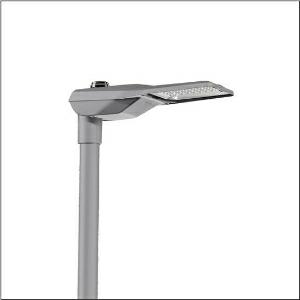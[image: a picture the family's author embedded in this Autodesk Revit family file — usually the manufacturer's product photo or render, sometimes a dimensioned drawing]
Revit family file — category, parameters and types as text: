
# Revit family: streetlight_sl_21_mini___pl52_5xe6h47n08hb_96c1
name_source: partatom
category: Lighting Fixtures
units: mm (PartAtom-declared; Revit-internal decimal feet)

## family parameters
Cut with Voids When Loaded = No
Host = Face
Light Source = No
Part Type = Normal
Room Calculation Point = No
Round Connector Dimension = Use Diameter
Shared = No

## types (1)
- --- (1 x LED, 9260 lm, 66 W, 4000K)
    Apparent Load = 66 VA
    CIE Flux Codes = 27 59 98 100 100
    Color Rendering = 70
    Color Temperature = 4000K
    Default Elevation = 1800 mm
    Description = Streetlight SL 21 mini, mast luminaire, primary light control with lens, of PMMA, primary optical cover: cover, of toughened safety glass, transparent, light distribution: PL52, light emission: direct distribution, primary light characteristic: asymmetric, installation type: side-entry, LED, 3G 1.5mm², High Power LED, rated luminous flux: 9.260lm, luminous efficacy: 140lm/W, light colour: 740, colour temperature: 4000K, control gear: NEMA (7pin), control: overheat protection, pre-setting: linear dimming characteristic, constant luminous flux control, time-dependent luminous flux control, flexible luminous flux parameterisation, mains connection: 230..240V, AC, 50/60Hz, connection cable pre-assembled, cable length: 8,5m, wiring characteristics: H07RN-F, start of lifetime: 66W, end of service life: 69W, reduction: 30W, luminaire housing, of diecast aluminium (EN AC-44300), powder-coated, SITECO metallic grey (DB 702S), corrosivity category C5 high according to DIN EN ISO 12944, multi-level sealing system, sealing non-destructively replaceable, inclination adjustable: 0°, 5°, 10°, 15°, length: 628mm, width: 235mm, height: 110mm, spigot size: 42mm (side-entry), mounting height: 4..8m, protection rating (complete): IP66, insulation class (complete): insulation class I (protective earthing), certification: CE, ENEC, ENEC+, VDE, impact resistance: IK10, permissible operating ambient temperature for outdoor applications: -40..+50°C, standard-compliant lighting for roads and squares, packaging unit: 1 piece

Light Distribution: PL52
    Height = 110 mm
    Lamp = 1 x LED
    Lamp Light Flux = 9260 lm
    Lamp Power = 66 W
    Lamp count = 1
    Length = 625 mm
    Luminous efficacy = 140 lm/W
    Manufacturer = Siteco
    ModVariant = No
    Model = 5XE6H47N08HB
    Number of Poles = 1
    OnlyDefault = Yes
    Power Factor = 1
    Product Name = Streetlight SL 21 mini | PL52
    Product group = mast luminaire | pylon top
    ProductGroupID = 6100
    Protection Class = Protection class I
    Protection Degree = IP 66
    RLX_Detail_Level = 1
    RLX_Emergency_Light_Flux = 0 lm
    RLX_Emergency_Type = 0
    RLX_Emergency_Type_DB = No
    RlxData = <blob elided: 35661 chars, md5=ec41a24c>
    Socket = socket
    Standby Power = 0 W
    System Light Flux = 9260 lm
    System Power = 66 W
    Type Comments = factory setting: luminous flux: 100 % | dim-lin: 254 | 670 mA
    Type Image = l_1294379.jpg
    URL = http://relux.com
    VarID = @adj_136461
    Voltage = 0 V
    Weight = 0.00 kg
    Width = 234 mm

## geometry (parser evidence)
native form markers: Blend x4, Sweep x11
no freeform markers — native parametric forms only
